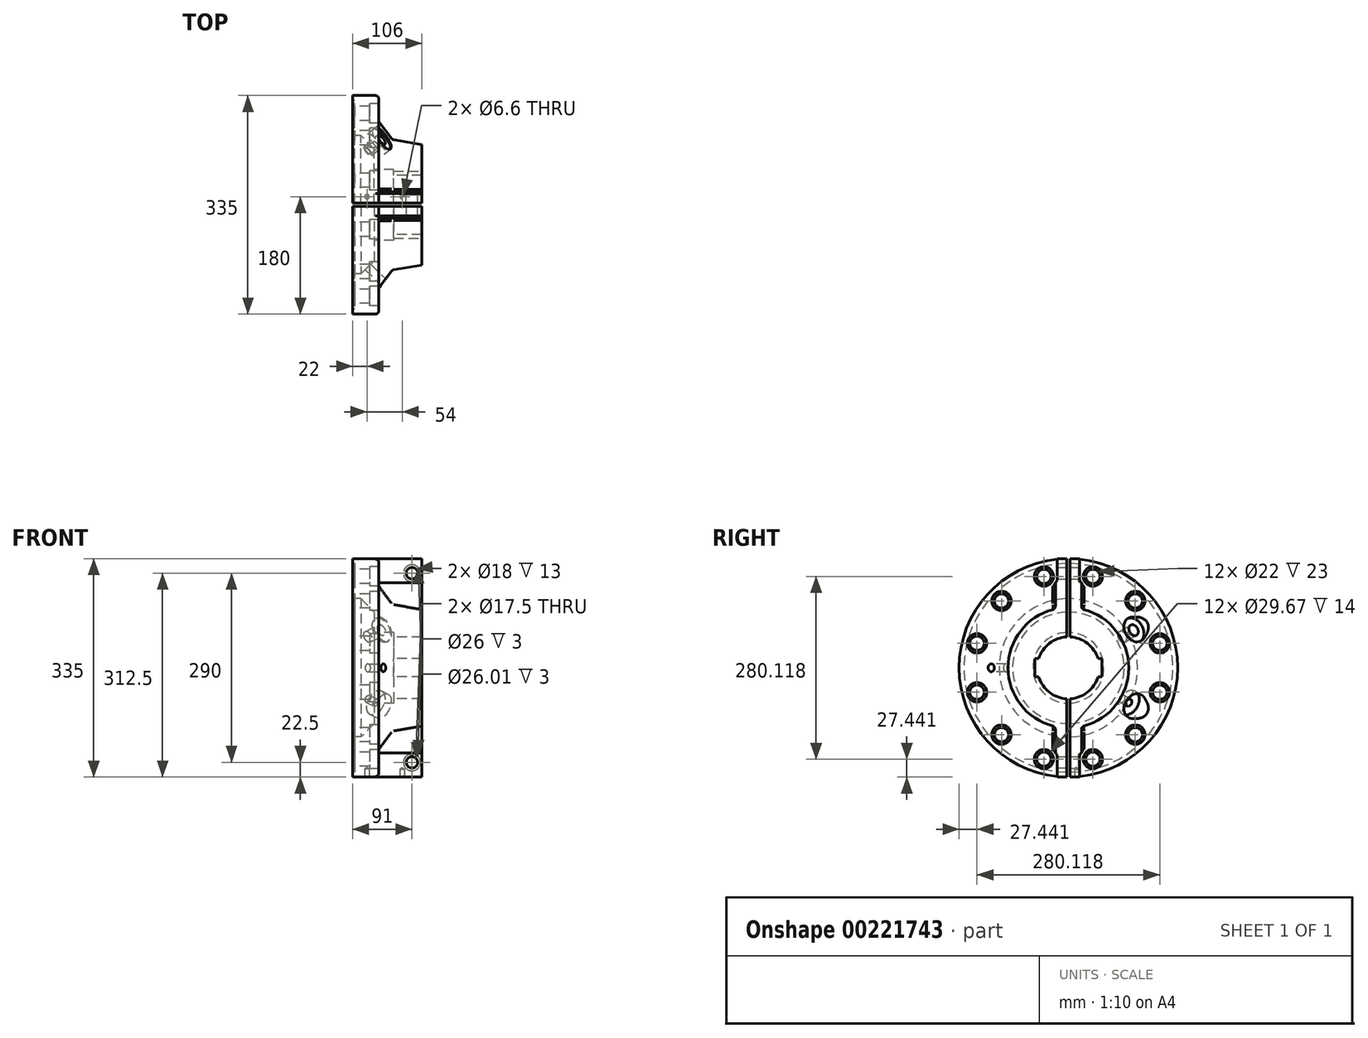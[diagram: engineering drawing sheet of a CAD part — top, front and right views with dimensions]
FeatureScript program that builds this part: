
annotation { "Feature Type Name" : "Feature", "Feature Type Description" : "" }
export const myFeature = defineFeature(function(context is Context, id is Id, definition is map)
    precondition{}
    {
        {
            var Q0;
            Q0=qCreatedBy(makeId("Front.planeOp"),FACE);
            var sketch = newSketch(context, id + "F0", { "sketchPlane" : qUnion([Q0])});
            skLineSegment(sketch, "E0", {"start": v(0, 0) * mm, "end": v(0, 167.5) * mm});
            skLineSegment(sketch, "E1", {"start": v(0, 167.5) * mm, "end": v(40, 167.5) * mm});
            skLineSegment(sketch, "E2", {"start": v(40, 167.5) * mm, "end": v(40, 127.5) * mm});
            skLineSegment(sketch, "E3", {"start": v(40, 127.5) * mm, "end": v(61, 100) * mm});
            skLineSegment(sketch, "E4", {"start": v(61, 100) * mm, "end": v(106, 92.5) * mm});
            skLineSegment(sketch, "E5", {"start": v(106, 92.5) * mm, "end": v(106, 0) * mm});
            skLineSegment(sketch, "E6", {"start": v(0, 0) * mm, "end": v(106, 0) * mm});
            skSolve(sketch);
        }
        {
            var Q0;
            Q0 = qSketchRegion(id + "F0", true);
            var Q1;
            Q1=sQuery(id+"F0.wireOp",EDGE,"E6");
            revolve(context, id + "F1", {"entities" : qUnion([Q0]), "axis" : qUnion([Q1]), "revolveType" : RevolveType.ONE_DIRECTION, "angle" : 180 * degree});
        }
        {
            var Q0;
            Q0=qCreatedBy(makeId("Front.planeOp"),FACE);
            var sketch = newSketch(context, id + "F2", { "sketchPlane" : qUnion([Q0])});
            skLineSegment(sketch, "E7.0", {"start": v(106, -167.5) * mm, "end": v(106, 167.97) * mm});
            skLineSegment(sketch, "E8.0", {"start": v(40, -167.5) * mm, "end": v(106, -167.5) * mm});
            skPoint(sketch, "E9.orphan", {"position": v(40, -167.5) * mm});
            skPoint(sketch, "E10.orphan", {"position": v(106, -92.5) * mm});
            skPoint(sketch, "E11.orphan", {"position": v(106, 92.5) * mm});
            skLineSegment(sketch, "E12.0", {"start": v(40, 167.5) * mm, "end": v(106, 167.5) * mm});
            skPoint(sketch, "E13.orphan", {"position": v(40, 167.5) * mm});
            skLineSegment(sketch, "E14.0", {"start": v(40, -167.5) * mm, "end": v(40, 167.5) * mm});
            skPoint(sketch, "E15.orphan", {"position": v(0, -167.5) * mm});
            skPoint(sketch, "E16.orphan", {"position": v(0, 167.5) * mm});
            skSolve(sketch);
        }
        {
            var Q0;
            Q0 = qSketchRegion(id + "F2", true);
            extrude(context, id + "F3", {"entities" : qUnion([Q0]), "operationType" : NewBodyOperationType.ADD, "depth" : 20 * mm});
        }
        {
            var Q0;
            Q0=makeQuery(id+"F3.boolean.opBoolean","MERGE",FACE,{"derivedFrom":[makeQuery(id+"F1.opRevolve","SWEPT_FACE",FACE,{"disambiguationData":[OSD([sQuery(id+"F0.wireOp",EDGE,"E5")])]}),makeQuery(id+"F3.opExtrude","SWEPT_FACE",FACE,{"disambiguationData":[OSD([sQuery(id+"F2.wireOp",EDGE,"E7.0")])]})]});
            var sketch = newSketch(context, id + "F4", { "sketchPlane" : qUnion([Q0])});
            skLineSegment(sketch, "E17.bottom", {"start": v(-20, -167.5) * mm, "end": v(-17, -167.5) * mm});
            skLineSegment(sketch, "E17.left", {"start": v(-20, -167.5) * mm, "end": v(-20, -130.36) * mm});
            skLineSegment(sketch, "E17.right", {"start": v(-17, -167.5) * mm, "end": v(-17, -137.5) * mm});
            skPoint(sketch, "E18.visualSharp", {"position": v(-17, -121.57) * mm});
            skArc(sketch, "E18.filletArc", {"start": v(-17, -137.5) * mm, "mid": v(-17.78, -133.63) * mm, "end": v(-20, -130.36) * mm});
            skLineSegment(sketch, "E19", {"start": v(0, 0) * mm, "end": v(-51.58, 0) * mm, "construction": true});
            skLineSegment(sketch, "E20.MirrorCS", {"start": v(-17, 167.5) * mm, "end": v(-17, 137.5) * mm});
            skLineSegment(sketch, "E21.MirrorCS", {"start": v(-20, 167.5) * mm, "end": v(-17, 167.5) * mm});
            skLineSegment(sketch, "E22.MirrorCS", {"start": v(-20, 167.5) * mm, "end": v(-20, 130.36) * mm});
            skArc(sketch, "E23.MirrorCS", {"start": v(-17, 137.5) * mm, "mid": v(-17.78, 133.63) * mm, "end": v(-20, 130.36) * mm});
            skSolve(sketch);
        }
        {
            var Q0;
            Q0 = qSketchRegion(id + "F4", true);
            extrude(context, id + "F5", {"entities" : qUnion([Q0]), "operationType" : NewBodyOperationType.REMOVE, "oppositeDirection" : true, "depth" : 66 * mm});
        }
        {
            var Q0;
            Q0=makeQuery(id+"F1.opRevolve","SWEPT_BODY",BODY,{"disambiguationData":[OSD([sQuery(id+"F0.wireOp",EDGE,"E0"),sQuery(id+"F0.wireOp",EDGE,"E1"),sQuery(id+"F0.wireOp",EDGE,"E2"),sQuery(id+"F0.wireOp",EDGE,"E3"),sQuery(id+"F0.wireOp",EDGE,"E4"),sQuery(id+"F0.wireOp",EDGE,"E5"),sQuery(id+"F0.wireOp",EDGE,"E6")])]});
            var Q1;
            Q1=qCreatedBy(makeId("Front.planeOp"),FACE);
            mirror(context, id + "F6", {"entities" : qUnion([Q0]), "mirrorPlane" : qUnion([Q1])});
        }
        {
            var Q0;
            Q0=makeQuery(id+"F6.opPattern","COPY",FACE,{"derivedFrom":makeQuery(id+"F1.opRevolve","SWEPT_FACE",FACE,{"disambiguationData":[OSD([sQuery(id+"F0.wireOp",EDGE,"E0")])]}),"instanceName":"1"});
            var sketch = newSketch(context, id + "F7", { "sketchPlane" : qUnion([Q0])});
            skLineSegment(sketch, "E24.bottom", {"start": v(-2.5, 185) * mm, "end": v(2.5, 185) * mm});
            skLineSegment(sketch, "E24.top", {"start": v(-2.5, -185) * mm, "end": v(2.5, -185) * mm});
            skLineSegment(sketch, "E24.left", {"start": v(-2.5, 185) * mm, "end": v(-2.5, -185) * mm});
            skLineSegment(sketch, "E24.right", {"start": v(2.5, 185) * mm, "end": v(2.5, -185) * mm});
            skPoint(sketch, "E24.middle", {"position": v(0, 0) * mm});
            skSolve(sketch);
        }
        {
            var Q0;
            Q0 = qSketchRegion(id + "F7", true);
            extrude(context, id + "F8", {"entities" : qUnion([Q0]), "operationType" : NewBodyOperationType.REMOVE, "endBound" : BoundingType.THROUGH_ALL, "oppositeDirection" : true, "depth" : 25 * mm});
        }
        {
            var Q0;
            Q0=qCreatedBy(makeId("Top.planeOp"),FACE);
            var sketch = newSketch(context, id + "F9", { "sketchPlane" : qUnion([Q0])});
            skLineSegment(sketch, "E25", {"start": v(0, 0) * mm, "end": v(0, 160) * mm});
            skLineSegment(sketch, "E26", {"start": v(0, 160) * mm, "end": v(3, 160) * mm});
            skLineSegment(sketch, "E27", {"start": v(3, 160) * mm, "end": v(3, 106) * mm});
            skLineSegment(sketch, "E28", {"start": v(3, 106) * mm, "end": v(13, 106) * mm});
            skLineSegment(sketch, "E29", {"start": v(13, 106) * mm, "end": v(33, 85.5) * mm});
            skLineSegment(sketch, "E30", {"start": v(33, 85.5) * mm, "end": v(33, 54.2) * mm});
            skLineSegment(sketch, "E31", {"start": v(33, 54.2) * mm, "end": v(63, 54.2) * mm});
            skLineSegment(sketch, "E32", {"start": v(63, 54.2) * mm, "end": v(63, 47.5) * mm});
            skLineSegment(sketch, "E33", {"start": v(63, 47.5) * mm, "end": v(106, 47.5) * mm});
            skLineSegment(sketch, "E34", {"start": v(106, 47.5) * mm, "end": v(106, 0) * mm});
            skLineSegment(sketch, "E35", {"start": v(106, 0) * mm, "end": v(0, 0) * mm});
            skSolve(sketch);
        }
        {
            var Q0;
            Q0 = qSketchRegion(id + "F9", true);
            var Q1;
            Q1=sQuery(id+"F9.wireOp",EDGE,"E35");
            revolve(context, id + "F10", {"operationType" : NewBodyOperationType.REMOVE, "entities" : qUnion([Q0]), "axis" : qUnion([Q1]), "revolveType" : RevolveType.FULL, "oppositeDirection" : true});
        }
        {
            var Q0;
            Q0=makeQuery(id+"F10.boolean.opBoolean","COPY",FACE,{"disambiguationData":[TD([makeQuery(id+"F8.boolean.opBoolean","COPY",FACE,{"derivedFrom":makeQuery(id+"F8.opExtrude","SWEPT_FACE",FACE,{"disambiguationData":[OSD([sQuery(id+"F7.wireOp",EDGE,"E24.right")])]})})])],"derivedFrom":makeQuery(id+"F10.opRevolve","SWEPT_FACE",FACE,{"disambiguationData":[OSD([sQuery(id+"F9.wireOp",EDGE,"E27")])]})});
            var sketch = newSketch(context, id + "F11", { "sketchPlane" : qUnion([Q0])});
            skCircle(sketch, "E36", {"center": v(37.53, 140.06) * mm, "radius": 11 * mm});
            skLineSegment(sketch, "E37", {"start": v(0, 0) * mm, "end": v(37.53, 140.06) * mm, "construction": true});
            skLineSegment(sketch, "E38", {"start": v(0, 0) * mm, "end": v(0, 41.16) * mm, "construction": true});
            skCircle(sketch, "E39.1.0", {"center": v(-37.53, 140.06) * mm, "radius": 11 * mm});
            skCircle(sketch, "E39.2.0", {"center": v(-102.53, 102.53) * mm, "radius": 11 * mm});
            skCircle(sketch, "E39.3.0", {"center": v(-140.06, 37.53) * mm, "radius": 11 * mm});
            skCircle(sketch, "E39.4.0", {"center": v(-140.06, -37.53) * mm, "radius": 11 * mm});
            skCircle(sketch, "E39.5.0", {"center": v(-102.53, -102.53) * mm, "radius": 11 * mm});
            skCircle(sketch, "E39.6.0", {"center": v(-37.53, -140.06) * mm, "radius": 11 * mm});
            skCircle(sketch, "E39.7.0", {"center": v(37.53, -140.06) * mm, "radius": 11 * mm});
            skCircle(sketch, "E39.8.0", {"center": v(102.53, -102.53) * mm, "radius": 11 * mm});
            skCircle(sketch, "E39.9.0", {"center": v(140.06, -37.53) * mm, "radius": 11 * mm});
            skCircle(sketch, "E39.10.0", {"center": v(140.06, 37.53) * mm, "radius": 11 * mm});
            skCircle(sketch, "E39.11.0", {"center": v(102.53, 102.53) * mm, "radius": 11 * mm});
            skPoint(sketch, "E39.center", {"position": v(0, 0) * mm});
            skCircle(sketch, "E40", {"center": v(37.53, 140.06) * mm, "radius": 14.84 * mm});
            skCircle(sketch, "E41", {"center": v(102.53, 102.53) * mm, "radius": 14.84 * mm});
            skCircle(sketch, "E42", {"center": v(140.06, 37.53) * mm, "radius": 14.84 * mm});
            skCircle(sketch, "E43", {"center": v(140.06, -37.53) * mm, "radius": 14.84 * mm});
            skCircle(sketch, "E44", {"center": v(102.53, -102.53) * mm, "radius": 14.84 * mm});
            skCircle(sketch, "E45", {"center": v(37.53, -140.06) * mm, "radius": 14.84 * mm});
            skCircle(sketch, "E46", {"center": v(-37.53, -140.06) * mm, "radius": 14.84 * mm});
            skCircle(sketch, "E47", {"center": v(-102.53, -102.53) * mm, "radius": 14.84 * mm});
            skCircle(sketch, "E48", {"center": v(-140.06, -37.53) * mm, "radius": 14.84 * mm});
            skCircle(sketch, "E49", {"center": v(-140.06, 37.53) * mm, "radius": 14.84 * mm});
            skCircle(sketch, "E50", {"center": v(-102.53, 102.53) * mm, "radius": 14.84 * mm});
            skCircle(sketch, "E51", {"center": v(-37.53, 140.06) * mm, "radius": 14.84 * mm});
            skSolve(sketch);
        }
        {
            var Q0;
            Q0=makeQuery(id+"F11.imprint","IMPRINT",FACE,{"disambiguationData":[TD([[makeQuery(id+"F11.imprint","IMPRINT",EDGE,{"derivedFrom":sQuery(id+"F11.wireOp",EDGE,"E39.1.0")}),1.0]])]});
            var Q1;
            Q1=makeQuery(id+"F11.imprint","IMPRINT",FACE,{"disambiguationData":[TD([[makeQuery(id+"F11.imprint","IMPRINT",EDGE,{"derivedFrom":sQuery(id+"F11.wireOp",EDGE,"E36")}),1.0]])]});
            var Q2;
            Q2=makeQuery(id+"F11.imprint","IMPRINT",FACE,{"disambiguationData":[TD([[makeQuery(id+"F11.imprint","IMPRINT",EDGE,{"derivedFrom":sQuery(id+"F11.wireOp",EDGE,"E39.11.0")}),1.0]])]});
            var Q3;
            Q3=makeQuery(id+"F11.imprint","IMPRINT",FACE,{"disambiguationData":[TD([[makeQuery(id+"F11.imprint","IMPRINT",EDGE,{"derivedFrom":sQuery(id+"F11.wireOp",EDGE,"E39.10.0")}),1.0]])]});
            var Q4;
            Q4=makeQuery(id+"F11.imprint","IMPRINT",FACE,{"disambiguationData":[TD([[makeQuery(id+"F11.imprint","IMPRINT",EDGE,{"derivedFrom":sQuery(id+"F11.wireOp",EDGE,"E39.8.0")}),1.0]])]});
            var Q5;
            Q5=makeQuery(id+"F11.imprint","IMPRINT",FACE,{"disambiguationData":[TD([[makeQuery(id+"F11.imprint","IMPRINT",EDGE,{"derivedFrom":sQuery(id+"F11.wireOp",EDGE,"E39.7.0")}),1.0]])]});
            var Q6;
            Q6=makeQuery(id+"F11.imprint","IMPRINT",FACE,{"disambiguationData":[TD([[makeQuery(id+"F11.imprint","IMPRINT",EDGE,{"derivedFrom":sQuery(id+"F11.wireOp",EDGE,"E39.6.0")}),1.0]])]});
            var Q7;
            Q7=makeQuery(id+"F11.imprint","IMPRINT",FACE,{"disambiguationData":[TD([[makeQuery(id+"F11.imprint","IMPRINT",EDGE,{"derivedFrom":sQuery(id+"F11.wireOp",EDGE,"E39.5.0")}),1.0]])]});
            var Q8;
            Q8=makeQuery(id+"F6.opPattern","COPY",FACE,{"derivedFrom":makeQuery(id+"F5.boolean.opBoolean","MERGE",FACE,{"derivedFrom":[makeQuery(id+"F1.opRevolve","SWEPT_FACE",FACE,{"disambiguationData":[OSD([sQuery(id+"F0.wireOp",EDGE,"E2")])]}),makeQuery(id+"F5.opExtrude","CAP_FACE",FACE,{"disambiguationData":[OSD([sQuery(id+"F4.wireOp",EDGE,"E17.bottom"),sQuery(id+"F4.wireOp",EDGE,"E17.left"),sQuery(id+"F4.wireOp",EDGE,"E17.right"),sQuery(id+"F4.wireOp",EDGE,"E18.filletArc")])],"isStart":false}),makeQuery(id+"F5.opExtrude","CAP_FACE",FACE,{"disambiguationData":[OSD([sQuery(id+"F4.wireOp",EDGE,"E20.MirrorCS"),sQuery(id+"F4.wireOp",EDGE,"E21.MirrorCS"),sQuery(id+"F4.wireOp",EDGE,"E22.MirrorCS"),sQuery(id+"F4.wireOp",EDGE,"E23.MirrorCS")])],"isStart":false})]}),"instanceName":"1"});
            var Q9;
            Q9=makeQuery(id+"F11.imprint","IMPRINT",FACE,{"disambiguationData":[TD([[makeQuery(id+"F11.imprint","IMPRINT",EDGE,{"derivedFrom":sQuery(id+"F11.wireOp",EDGE,"E39.4.0")}),1.0]])]});
            var Q10;
            Q10=makeQuery(id+"F11.imprint","IMPRINT",FACE,{"disambiguationData":[TD([[makeQuery(id+"F11.imprint","IMPRINT",EDGE,{"derivedFrom":sQuery(id+"F11.wireOp",EDGE,"E39.2.0")}),1.0]])]});
            var Q11;
            Q11=makeQuery(id+"F11.imprint","IMPRINT",FACE,{"disambiguationData":[TD([[makeQuery(id+"F11.imprint","IMPRINT",EDGE,{"derivedFrom":sQuery(id+"F11.wireOp",EDGE,"E39.3.0")}),1.0]])]});
            var Q12;
            Q12=makeQuery(id+"F11.imprint","IMPRINT",FACE,{"disambiguationData":[TD([[makeQuery(id+"F11.imprint","IMPRINT",EDGE,{"derivedFrom":sQuery(id+"F11.wireOp",EDGE,"E39.9.0")}),1.0]])]});
            extrude(context, id + "F12", {"entities" : qUnion([Q0, Q1, Q2, Q3, Q4, Q5, Q6, Q7, Q8, Q9, Q10, Q11, Q12]), "operationType" : NewBodyOperationType.REMOVE, "endBound" : BoundingType.THROUGH_ALL, "oppositeDirection" : true, "depth" : 25 * mm});
        }
        {
            var Q0;
            Q0=qCreatedBy(makeId("Front.planeOp"),FACE);
            var sketch = newSketch(context, id + "F13", { "sketchPlane" : qUnion([Q0])});
            skCircle(sketch, "E52", {"center": v(91, 145) * mm, "radius": 7 * mm});
            skLineSegment(sketch, "E53", {"start": v(2.74, 0) * mm, "end": v(116.17, 0) * mm, "construction": true});
            skCircle(sketch, "E54.MirrorC", {"center": v(91, -145) * mm, "radius": 7 * mm});
            skSolve(sketch);
        }
        {
            var Q0;
            Q0 = qSketchRegion(id + "F13", true);
            extrude(context, id + "F14", {"entities" : qUnion([Q0]), "operationType" : NewBodyOperationType.REMOVE, "depth" : 17 * mm});
        }
        {
            var Q0;
            Q0=makeQuery(id+"F6.opPattern","COPY",FACE,{"derivedFrom":makeQuery(id+"F5.boolean.opBoolean","COPY",FACE,{"derivedFrom":makeQuery(id+"F5.opExtrude","SWEPT_FACE",FACE,{"disambiguationData":[OSD([sQuery(id+"F4.wireOp",EDGE,"E20.MirrorCS")])]})}),"instanceName":"1"});
            var sketch = newSketch(context, id + "F15", { "sketchPlane" : qUnion([Q0])});
            skCircle(sketch, "E55", {"center": v(-91, -145) * mm, "radius": 9 * mm});
            skCircle(sketch, "E56", {"center": v(-91, 145) * mm, "radius": 9 * mm});
            skCircle(sketch, "E57", {"center": v(-91, -145) * mm, "radius": 13 * mm});
            skCircle(sketch, "E58", {"center": v(-91, 145) * mm, "radius": 13 * mm});
            skSolve(sketch);
        }
        {
            var Q0;
            {var subQ0=sQuery(id+"F0.wireOp",EDGE,"E1");var subQ1=sQuery(id+"F0.wireOp",EDGE,"E2");Q0=makeQuery(id+"F3.boolean.opBoolean","SPLIT",EDGE,{"disambiguationData":[topologyDisambiguationEdgeConnected([makeQuery(id+"F1.opRevolve","SWEPT_FACE",FACE,{"disambiguationData":[OSD([subQ0])]}),makeQuery(id+"F1.opRevolve","SWEPT_FACE",FACE,{"disambiguationData":[OSD([subQ1])]})])],"derivedFrom":makeQuery(id+"F1.opRevolve","SWEPT_EDGE",EDGE,{"disambiguationData":[OSD([subQ0,subQ1])]})});}
            var Q1;
            Q1=makeQuery(id+"F1.opRevolve","SWEPT_EDGE",EDGE,{"disambiguationData":[OSD([sQuery(id+"F0.wireOp",EDGE,"E2"),sQuery(id+"F0.wireOp",EDGE,"E3")])]});
            var Q2;
            Q2=makeQuery(id+"F1.opRevolve","SWEPT_EDGE",EDGE,{"disambiguationData":[OSD([sQuery(id+"F0.wireOp",EDGE,"E3"),sQuery(id+"F0.wireOp",EDGE,"E4")])]});
            var Q3;
            Q3=makeQuery(id+"F3.boolean.opBoolean","INTERSECT",EDGE,{"disambiguationData":[OD(0.0)],"derivedFrom":[makeQuery(id+"F1.opRevolve","SWEPT_FACE",FACE,{"disambiguationData":[OSD([sQuery(id+"F0.wireOp",EDGE,"E4")])]}),makeQuery(id+"F3.opExtrude","CAP_FACE",FACE,{"disambiguationData":[OSD([sQuery(id+"F2.wireOp",EDGE,"E7.0"),sQuery(id+"F2.wireOp",EDGE,"E8.0"),sQuery(id+"F2.wireOp",EDGE,"E12.0"),sQuery(id+"F2.wireOp",EDGE,"E14.0")])],"isStart":false})]});
            var Q4;
            Q4=makeQuery(id+"F3.boolean.opBoolean","INTERSECT",EDGE,{"disambiguationData":[OD(1.0)],"derivedFrom":[makeQuery(id+"F1.opRevolve","SWEPT_FACE",FACE,{"disambiguationData":[OSD([sQuery(id+"F0.wireOp",EDGE,"E4")])]}),makeQuery(id+"F3.opExtrude","CAP_FACE",FACE,{"disambiguationData":[OSD([sQuery(id+"F2.wireOp",EDGE,"E7.0"),sQuery(id+"F2.wireOp",EDGE,"E8.0"),sQuery(id+"F2.wireOp",EDGE,"E12.0"),sQuery(id+"F2.wireOp",EDGE,"E14.0")])],"isStart":false})]});
            var Q5;
            Q5=makeQuery(id+"F3.boolean.opBoolean","INTERSECT",EDGE,{"disambiguationData":[OD(0.0)],"derivedFrom":[makeQuery(id+"F1.opRevolve","SWEPT_FACE",FACE,{"disambiguationData":[OSD([sQuery(id+"F0.wireOp",EDGE,"E3")])]}),makeQuery(id+"F3.opExtrude","CAP_FACE",FACE,{"disambiguationData":[OSD([sQuery(id+"F2.wireOp",EDGE,"E7.0"),sQuery(id+"F2.wireOp",EDGE,"E8.0"),sQuery(id+"F2.wireOp",EDGE,"E12.0"),sQuery(id+"F2.wireOp",EDGE,"E14.0")])],"isStart":false})]});
            var Q6;
            Q6=makeQuery(id+"F3.boolean.opBoolean","INTERSECT",EDGE,{"disambiguationData":[OD(1.0)],"derivedFrom":[makeQuery(id+"F1.opRevolve","SWEPT_FACE",FACE,{"disambiguationData":[OSD([sQuery(id+"F0.wireOp",EDGE,"E3")])]}),makeQuery(id+"F3.opExtrude","CAP_FACE",FACE,{"disambiguationData":[OSD([sQuery(id+"F2.wireOp",EDGE,"E7.0"),sQuery(id+"F2.wireOp",EDGE,"E8.0"),sQuery(id+"F2.wireOp",EDGE,"E12.0"),sQuery(id+"F2.wireOp",EDGE,"E14.0")])],"isStart":false})]});
            var Q7;
            {var subQ0=sQuery(id+"F0.wireOp",EDGE,"E1");var subQ1=makeQuery(id+"F1.opRevolve","SWEPT_FACE",FACE,{"disambiguationData":[OSD([subQ0])]});var subQ2=sQuery(id+"F0.wireOp",EDGE,"E2");var subQ3=makeQuery(id+"F1.opRevolve","SWEPT_FACE",FACE,{"disambiguationData":[OSD([subQ2])]});var subQ4=makeQuery(id+"F1.opRevolve","SWEPT_EDGE",EDGE,{"disambiguationData":[OSD([subQ0,subQ2])]});var subQ5=sQuery(id+"F2.wireOp",EDGE,"E14.0");var subQ6=sQuery(id+"F2.wireOp",EDGE,"E12.0");var subQ7=sQuery(id+"F2.wireOp",EDGE,"E8.0");var subQ12=makeQuery(id+"F3.opExtrude","SWEPT_FACE",FACE,{"disambiguationData":[OSD([subQ5])]});Q7=makeQuery(id+"F6.opPattern","COPY",EDGE,{"derivedFrom":makeQuery(id+"F5.boolean.opBoolean","MERGE",EDGE,{"derivedFrom":[makeQuery(id+"F3.boolean.opBoolean","SPLIT",EDGE,{"disambiguationData":[topologyDisambiguationEdgeConnected([subQ1,subQ12]),TD([makeQuery(id+"F3.opExtrude","SWEPT_FACE",FACE,{"disambiguationData":[OSD([subQ6])]})])],"derivedFrom":subQ4}),makeQuery(id+"F3.boolean.opBoolean","SPLIT",EDGE,{"disambiguationData":[topologyDisambiguationEdgeConnected([subQ1,subQ12]),TD([makeQuery(id+"F3.opExtrude","SWEPT_FACE",FACE,{"disambiguationData":[OSD([subQ7])]})])],"derivedFrom":subQ4}),makeQuery(id+"F3.boolean.opBoolean","SPLIT",EDGE,{"disambiguationData":[topologyDisambiguationEdgeConnected([subQ1,subQ3])],"derivedFrom":subQ4})]}),"instanceName":"1"});}
            var Q8;
            Q8=makeQuery(id+"F6.opPattern","COPY",EDGE,{"derivedFrom":makeQuery(id+"F1.opRevolve","SWEPT_EDGE",EDGE,{"disambiguationData":[OSD([sQuery(id+"F0.wireOp",EDGE,"E2"),sQuery(id+"F0.wireOp",EDGE,"E3")])]}),"instanceName":"1"});
            var Q9;
            Q9=makeQuery(id+"F6.opPattern","COPY",EDGE,{"derivedFrom":makeQuery(id+"F1.opRevolve","SWEPT_EDGE",EDGE,{"disambiguationData":[OSD([sQuery(id+"F0.wireOp",EDGE,"E3"),sQuery(id+"F0.wireOp",EDGE,"E4")])]}),"instanceName":"1"});
            var Q10;
            Q10=makeQuery(id+"F6.opPattern","COPY",EDGE,{"derivedFrom":makeQuery(id+"F3.boolean.opBoolean","INTERSECT",EDGE,{"disambiguationData":[OD(0.0)],"derivedFrom":[makeQuery(id+"F1.opRevolve","SWEPT_FACE",FACE,{"disambiguationData":[OSD([sQuery(id+"F0.wireOp",EDGE,"E4")])]}),makeQuery(id+"F3.opExtrude","CAP_FACE",FACE,{"disambiguationData":[OSD([sQuery(id+"F2.wireOp",EDGE,"E7.0"),sQuery(id+"F2.wireOp",EDGE,"E8.0"),sQuery(id+"F2.wireOp",EDGE,"E12.0"),sQuery(id+"F2.wireOp",EDGE,"E14.0")])],"isStart":false})]}),"instanceName":"1"});
            var Q11;
            Q11=makeQuery(id+"F6.opPattern","COPY",EDGE,{"derivedFrom":makeQuery(id+"F3.boolean.opBoolean","INTERSECT",EDGE,{"disambiguationData":[OD(0.0)],"derivedFrom":[makeQuery(id+"F1.opRevolve","SWEPT_FACE",FACE,{"disambiguationData":[OSD([sQuery(id+"F0.wireOp",EDGE,"E3")])]}),makeQuery(id+"F3.opExtrude","CAP_FACE",FACE,{"disambiguationData":[OSD([sQuery(id+"F2.wireOp",EDGE,"E7.0"),sQuery(id+"F2.wireOp",EDGE,"E8.0"),sQuery(id+"F2.wireOp",EDGE,"E12.0"),sQuery(id+"F2.wireOp",EDGE,"E14.0")])],"isStart":false})]}),"instanceName":"1"});
            var Q12;
            Q12=makeQuery(id+"F6.opPattern","COPY",EDGE,{"derivedFrom":makeQuery(id+"F3.boolean.opBoolean","INTERSECT",EDGE,{"disambiguationData":[OD(1.0)],"derivedFrom":[makeQuery(id+"F1.opRevolve","SWEPT_FACE",FACE,{"disambiguationData":[OSD([sQuery(id+"F0.wireOp",EDGE,"E3")])]}),makeQuery(id+"F3.opExtrude","CAP_FACE",FACE,{"disambiguationData":[OSD([sQuery(id+"F2.wireOp",EDGE,"E7.0"),sQuery(id+"F2.wireOp",EDGE,"E8.0"),sQuery(id+"F2.wireOp",EDGE,"E12.0"),sQuery(id+"F2.wireOp",EDGE,"E14.0")])],"isStart":false})]}),"instanceName":"1"});
            var Q13;
            Q13=makeQuery(id+"F6.opPattern","COPY",EDGE,{"derivedFrom":makeQuery(id+"F3.boolean.opBoolean","INTERSECT",EDGE,{"disambiguationData":[OD(1.0)],"derivedFrom":[makeQuery(id+"F1.opRevolve","SWEPT_FACE",FACE,{"disambiguationData":[OSD([sQuery(id+"F0.wireOp",EDGE,"E4")])]}),makeQuery(id+"F3.opExtrude","CAP_FACE",FACE,{"disambiguationData":[OSD([sQuery(id+"F2.wireOp",EDGE,"E7.0"),sQuery(id+"F2.wireOp",EDGE,"E8.0"),sQuery(id+"F2.wireOp",EDGE,"E12.0"),sQuery(id+"F2.wireOp",EDGE,"E14.0")])],"isStart":false})]}),"instanceName":"1"});
            fillet(context, id + "F16", {"entities" : qUnion([Q0, Q1, Q2, Q3, Q4, Q5, Q6, Q7, Q8, Q9, Q10, Q11, Q12, Q13]), "radius" : 5 * mm, "tangentPropagation" : true, "allowEdgeOverflow" : false});
        }
        {
            var Q0;
            {var subQ0=sQuery(id+"F15.wireOp",EDGE,"E56");var subQ1=makeQuery(id+"F6.opPattern","COPY",EDGE,{"derivedFrom":makeQuery(id+"F5.boolean.opBoolean","COPY",EDGE,{"derivedFrom":makeQuery(id+"F5.opExtrude","SWEPT_EDGE",EDGE,{"disambiguationData":[OSD([sQuery(id+"F4.wireOp",EDGE,"E20.MirrorCS"),sQuery(id+"F4.wireOp",EDGE,"E23.MirrorCS")])]})}),"instanceName":"1"});var subQ2=makeQuery(id+"F15.imprint","INTERSECT",VERTEX,{"disambiguationData":[OD(0.0)],"derivedFrom":[subQ1,subQ0]});Q0=makeQuery(id+"F15.imprint","IMPRINT",FACE,{"disambiguationData":[TD([[makeQuery(id+"F15.imprint","IMPRINT",EDGE,{"disambiguationData":[TD([[subQ2,1.0]])],"derivedFrom":subQ0}),1.0]])]});}
            var Q1;
            Q1=makeQuery(id+"F15.imprint","IMPRINT",FACE,{"disambiguationData":[TD([[makeQuery(id+"F15.imprint","IMPRINT",EDGE,{"derivedFrom":sQuery(id+"F15.wireOp",EDGE,"E55")}),1.0]])]});
            var Q2;
            {var subQ0=sQuery(id+"F15.wireOp",EDGE,"E56");var subQ1=makeQuery(id+"F6.opPattern","COPY",EDGE,{"derivedFrom":makeQuery(id+"F5.boolean.opBoolean","COPY",EDGE,{"derivedFrom":makeQuery(id+"F5.opExtrude","SWEPT_EDGE",EDGE,{"disambiguationData":[OSD([sQuery(id+"F4.wireOp",EDGE,"E20.MirrorCS"),sQuery(id+"F4.wireOp",EDGE,"E23.MirrorCS")])]})}),"instanceName":"1"});var subQ2=makeQuery(id+"F15.imprint","INTERSECT",VERTEX,{"disambiguationData":[OD(0.0)],"derivedFrom":[subQ1,subQ0]});Q2=makeQuery(id+"F15.imprint","IMPRINT",FACE,{"disambiguationData":[TD([[makeQuery(id+"F15.imprint","IMPRINT",EDGE,{"disambiguationData":[TD([[subQ2,-1.0]])],"derivedFrom":subQ0}),1.0]])]});}
            extrude(context, id + "F17", {"entities" : qUnion([Q0, Q1, Q2]), "operationType" : NewBodyOperationType.REMOVE, "oppositeDirection" : true, "depth" : 17 * mm, "hasSecondDirection" : true, "secondDirectionOppositeDirection" : false, "secondDirectionDepth" : 25 * mm});
        }
        {
            var Q0;
            {var subQ0=sQuery(id+"F15.wireOp",EDGE,"E56");var subQ1=makeQuery(id+"F6.opPattern","COPY",EDGE,{"derivedFrom":makeQuery(id+"F5.boolean.opBoolean","COPY",EDGE,{"derivedFrom":makeQuery(id+"F5.opExtrude","SWEPT_EDGE",EDGE,{"disambiguationData":[OSD([sQuery(id+"F4.wireOp",EDGE,"E20.MirrorCS"),sQuery(id+"F4.wireOp",EDGE,"E23.MirrorCS")])]})}),"instanceName":"1"});var subQ2=makeQuery(id+"F15.imprint","INTERSECT",VERTEX,{"disambiguationData":[OD(0.0)],"derivedFrom":[subQ1,subQ0]});Q0=makeQuery(id+"F15.imprint","IMPRINT",FACE,{"disambiguationData":[TD([[makeQuery(id+"F15.imprint","IMPRINT",EDGE,{"disambiguationData":[TD([[subQ2,-1.0]])],"derivedFrom":subQ0}),-1.0]])]});}
            var Q1;
            {var subQ0=sQuery(id+"F15.wireOp",EDGE,"E56");var subQ1=makeQuery(id+"F6.opPattern","COPY",EDGE,{"derivedFrom":makeQuery(id+"F5.boolean.opBoolean","COPY",EDGE,{"derivedFrom":makeQuery(id+"F5.opExtrude","SWEPT_EDGE",EDGE,{"disambiguationData":[OSD([sQuery(id+"F4.wireOp",EDGE,"E20.MirrorCS"),sQuery(id+"F4.wireOp",EDGE,"E23.MirrorCS")])]})}),"instanceName":"1"});var subQ2=makeQuery(id+"F15.imprint","INTERSECT",VERTEX,{"disambiguationData":[OD(0.0)],"derivedFrom":[subQ1,subQ0]});Q1=makeQuery(id+"F15.imprint","IMPRINT",FACE,{"disambiguationData":[TD([[makeQuery(id+"F15.imprint","IMPRINT",EDGE,{"disambiguationData":[TD([[subQ2,1.0]])],"derivedFrom":subQ0}),-1.0]])]});}
            var Q2;
            Q2=makeQuery(id+"F15.imprint","IMPRINT",FACE,{"disambiguationData":[TD([[makeQuery(id+"F15.imprint","IMPRINT",EDGE,{"derivedFrom":sQuery(id+"F15.wireOp",EDGE,"E55")}),-1.0]])]});
            extrude(context, id + "F18", {"entities" : qUnion([Q0, Q1, Q2]), "operationType" : NewBodyOperationType.REMOVE, "endBound" : BoundingType.SYMMETRIC, "oppositeDirection" : true, "depth" : 3 * mm});
        }
        {
            var Q0;
            Q0=makeQuery(id+"F11.imprint","IMPRINT",FACE,{"disambiguationData":[TD([[makeQuery(id+"F11.imprint","IMPRINT",EDGE,{"derivedFrom":sQuery(id+"F11.wireOp",EDGE,"E39.1.0")}),-1.0]])]});
            var Q1;
            Q1=makeQuery(id+"F11.imprint","IMPRINT",FACE,{"disambiguationData":[TD([[makeQuery(id+"F11.imprint","IMPRINT",EDGE,{"derivedFrom":sQuery(id+"F11.wireOp",EDGE,"E39.2.0")}),-1.0]])]});
            var Q2;
            Q2=makeQuery(id+"F11.imprint","IMPRINT",FACE,{"disambiguationData":[TD([[makeQuery(id+"F11.imprint","IMPRINT",EDGE,{"derivedFrom":sQuery(id+"F11.wireOp",EDGE,"E39.3.0")}),-1.0]])]});
            var Q3;
            Q3=makeQuery(id+"F11.imprint","IMPRINT",FACE,{"disambiguationData":[TD([[makeQuery(id+"F11.imprint","IMPRINT",EDGE,{"derivedFrom":sQuery(id+"F11.wireOp",EDGE,"E36")}),-1.0]])]});
            var Q4;
            Q4=makeQuery(id+"F11.imprint","IMPRINT",FACE,{"disambiguationData":[TD([[makeQuery(id+"F11.imprint","IMPRINT",EDGE,{"derivedFrom":sQuery(id+"F11.wireOp",EDGE,"E39.11.0")}),-1.0]])]});
            var Q5;
            Q5=makeQuery(id+"F11.imprint","IMPRINT",FACE,{"disambiguationData":[TD([[makeQuery(id+"F11.imprint","IMPRINT",EDGE,{"derivedFrom":sQuery(id+"F11.wireOp",EDGE,"E39.10.0")}),-1.0]])]});
            var Q6;
            Q6=makeQuery(id+"F11.imprint","IMPRINT",FACE,{"disambiguationData":[TD([[makeQuery(id+"F11.imprint","IMPRINT",EDGE,{"derivedFrom":sQuery(id+"F11.wireOp",EDGE,"E39.4.0")}),-1.0]])]});
            var Q7;
            Q7=makeQuery(id+"F11.imprint","IMPRINT",FACE,{"disambiguationData":[TD([[makeQuery(id+"F11.imprint","IMPRINT",EDGE,{"derivedFrom":sQuery(id+"F11.wireOp",EDGE,"E39.5.0")}),-1.0]])]});
            var Q8;
            Q8=makeQuery(id+"F11.imprint","IMPRINT",FACE,{"disambiguationData":[TD([[makeQuery(id+"F11.imprint","IMPRINT",EDGE,{"derivedFrom":sQuery(id+"F11.wireOp",EDGE,"E39.6.0")}),-1.0]])]});
            var Q9;
            Q9=makeQuery(id+"F11.imprint","IMPRINT",FACE,{"disambiguationData":[TD([[makeQuery(id+"F11.imprint","IMPRINT",EDGE,{"derivedFrom":sQuery(id+"F11.wireOp",EDGE,"E39.8.0")}),-1.0]])]});
            var Q10;
            Q10=makeQuery(id+"F11.imprint","IMPRINT",FACE,{"disambiguationData":[TD([[makeQuery(id+"F11.imprint","IMPRINT",EDGE,{"derivedFrom":sQuery(id+"F11.wireOp",EDGE,"E39.9.0")}),-1.0]])]});
            var Q11;
            Q11=makeQuery(id+"F11.imprint","IMPRINT",FACE,{"disambiguationData":[TD([[makeQuery(id+"F11.imprint","IMPRINT",EDGE,{"derivedFrom":sQuery(id+"F11.wireOp",EDGE,"E39.7.0")}),-1.0]])]});
            var Q12;
            Q12=makeQuery(id+"F6.opPattern","COPY",FACE,{"derivedFrom":makeQuery(id+"F5.boolean.opBoolean","MERGE",FACE,{"derivedFrom":[makeQuery(id+"F1.opRevolve","SWEPT_FACE",FACE,{"disambiguationData":[OSD([sQuery(id+"F0.wireOp",EDGE,"E2")])]}),makeQuery(id+"F5.opExtrude","CAP_FACE",FACE,{"disambiguationData":[OSD([sQuery(id+"F4.wireOp",EDGE,"E17.bottom"),sQuery(id+"F4.wireOp",EDGE,"E17.left"),sQuery(id+"F4.wireOp",EDGE,"E17.right"),sQuery(id+"F4.wireOp",EDGE,"E18.filletArc")])],"isStart":false}),makeQuery(id+"F5.opExtrude","CAP_FACE",FACE,{"disambiguationData":[OSD([sQuery(id+"F4.wireOp",EDGE,"E20.MirrorCS"),sQuery(id+"F4.wireOp",EDGE,"E21.MirrorCS"),sQuery(id+"F4.wireOp",EDGE,"E22.MirrorCS"),sQuery(id+"F4.wireOp",EDGE,"E23.MirrorCS")])],"isStart":false})]}),"instanceName":"1"});
            extrude(context, id + "F19", {"entities" : qUnion([Q0, Q1, Q2, Q3, Q4, Q5, Q6, Q7, Q8, Q9, Q10, Q11]), "operationType" : NewBodyOperationType.REMOVE, "endBound" : BoundingType.THROUGH_ALL, "oppositeDirection" : true, "depth" : 23 * mm, "hasSecondDirection" : true, "secondDirectionOppositeDirection" : true, "secondDirectionBoundEntityFace" : qUnion([Q12]), "secondDirectionDepth" : 23 * mm});
        }
        {
            var Q0;
            Q0=makeQuery(id+"F3.boolean.opBoolean","MERGE",FACE,{"derivedFrom":[makeQuery(id+"F1.opRevolve","SWEPT_FACE",FACE,{"disambiguationData":[OSD([sQuery(id+"F0.wireOp",EDGE,"E5")])]}),makeQuery(id+"F3.opExtrude","SWEPT_FACE",FACE,{"disambiguationData":[OSD([sQuery(id+"F2.wireOp",EDGE,"E7.0")])]})]});
            var sketch = newSketch(context, id + "F20", { "sketchPlane" : qUnion([Q0])});
            skLineSegment(sketch, "E59.bottom", {"start": v(-51.4, -14) * mm, "end": v(51.4, -14) * mm});
            skLineSegment(sketch, "E59.top", {"start": v(-51.4, 14) * mm, "end": v(51.4, 14) * mm});
            skLineSegment(sketch, "E59.left", {"start": v(-51.4, -14) * mm, "end": v(-51.4, 14) * mm});
            skLineSegment(sketch, "E59.right", {"start": v(51.4, -14) * mm, "end": v(51.4, 14) * mm});
            skSolve(sketch);
        }
        {
            var Q0;
            Q0 = qSketchRegion(id + "F20", true);
            extrude(context, id + "F21", {"entities" : qUnion([Q0]), "operationType" : NewBodyOperationType.REMOVE, "endBound" : BoundingType.THROUGH_ALL, "oppositeDirection" : true, "depth" : 25 * mm});
        }
        {
            var Q0;
            Q0=makeQuery(id+"F6.opPattern","COPY",FACE,{"derivedFrom":makeQuery(id+"F3.opExtrude","SWEPT_FACE",FACE,{"disambiguationData":[OSD([sQuery(id+"F2.wireOp",EDGE,"E8.0")])]}),"instanceName":"1"});
            var sketch = newSketch(context, id + "F22", { "sketchPlane" : qUnion([Q0])});
            skCircle(sketch, "E60", {"center": v(76, -12.5) * mm, "radius": 3 * mm});
            skCircle(sketch, "E61", {"center": v(22, -12.5) * mm, "radius": 3 * mm});
            skSolve(sketch);
        }
        {
            var Q0;
            Q0 = qSketchRegion(id + "F22", true);
            extrude(context, id + "F23", {"entities" : qUnion([Q0]), "operationType" : NewBodyOperationType.REMOVE, "oppositeDirection" : true, "depth" : 10 * mm});
        }
        {
            var Q0;
            Q0=qCreatedBy(makeId("Top.planeOp"),FACE);
            var sketch = newSketch(context, id + "F24", { "sketchPlane" : qUnion([Q0])});
            skLineSegment(sketch, "E62.MirrorCS", {"start": v(13.28, -106.06) * mm, "end": v(33.08, -85.77) * mm});
            skLineSegment(sketch, "E63.MirrorCS", {"start": v(23.65, -95.44) * mm, "end": v(67.75, -138.46) * mm, "construction": true});
            skSolve(sketch);
        }
        {
            var Q0;
            Q0=sQuery(id+"F24.wireOp",EDGE,"E63.MirrorCS");
            var Q1;
            Q1=sQuery(id+"F24.wireOp",VERTEX,"E63.MirrorCS.end");
            cPlane(context, id + "F25", {"entities" : qUnion([Q0, Q1]), "cplaneType" : CPlaneType.LINE_POINT, "offset" : 25 * mm, "width" : 150 * mm, "height" : 150 * mm});
        }
        {
            var Q0;
            Q0=qCreatedBy(id+"F25.planeOp",FACE);
            var sketch = newSketch(context, id + "F26", { "sketchPlane" : qUnion([Q0])});
            skCircle(sketch, "E64", {"center": v(-51.8, 0) * mm, "radius": 6 * mm});
            skSolve(sketch);
        }
        {
            var Q0;
            Q0 = qSketchRegion(id + "F26", true);
            extrude(context, id + "F27", {"entities" : qUnion([Q0]), "endBound" : BoundingType.THROUGH_ALL, "oppositeDirection" : true, "depth" : 25 * mm});
        }
        {
            var Q0;
            Q0=makeQuery(id+"F27.opExtrude","SWEPT_BODY",BODY,{"disambiguationData":[OSD([sQuery(id+"F26.wireOp",EDGE,"E64")])]});
            var Q1;
            Q1=sQuery(id+"F9.wireOp",EDGE,"E35");
            transform(context, id + "F28", {"entities" : qUnion([Q0]), "transformType" : TransformType.ROTATION, "transformAxis" : qUnion([Q1]), "angle" : 150 * degree, "makeCopy" : true});
        }
        {
            var Q0;
            Q0=makeQuery(id+"F27.opExtrude","SWEPT_BODY",BODY,{"disambiguationData":[OSD([sQuery(id+"F26.wireOp",EDGE,"E64")])]});
            var Q1;
            Q1=sQuery(id+"F9.wireOp",EDGE,"E35");
            transform(context, id + "F29", {"entities" : qUnion([Q0]), "transformType" : TransformType.ROTATION, "transformAxis" : qUnion([Q1]), "angle" : 210 * degree, "makeCopy" : true});
        }
        {
            var Q0;
            Q0=makeQuery(id+"F27.opExtrude","SWEPT_BODY",BODY,{"disambiguationData":[OSD([sQuery(id+"F26.wireOp",EDGE,"E64")])]});
            var Q1;
            Q1=makeQuery(id+"F1.opRevolve","SWEPT_BODY",BODY,{"disambiguationData":[OSD([sQuery(id+"F0.wireOp",EDGE,"E0"),sQuery(id+"F0.wireOp",EDGE,"E1"),sQuery(id+"F0.wireOp",EDGE,"E2"),sQuery(id+"F0.wireOp",EDGE,"E3"),sQuery(id+"F0.wireOp",EDGE,"E4"),sQuery(id+"F0.wireOp",EDGE,"E5"),sQuery(id+"F0.wireOp",EDGE,"E6")])]});
            booleanBodies(context, id + "F30", {"operationType" : BooleanOperationType.SUBTRACTION, "tools" : qUnion([Q0]), "targets" : qUnion([Q1])});
        }
        {
            var Q0;
            Q0=makeQuery(id+"F29.opPattern","COPY",FACE,{"derivedFrom":makeQuery(id+"F27.opExtrude","CAP_FACE",FACE,{"disambiguationData":[OSD([sQuery(id+"F26.wireOp",EDGE,"E64")])],"isStart":true}),"instanceName":"1"});
            var sketch = newSketch(context, id + "F31", { "sketchPlane" : qUnion([Q0])});
            skCircle(sketch, "E65", {"center": v(40.32, -32.52) * mm, "radius": 6 * mm});
            skCircle(sketch, "E66", {"center": v(40.32, -32.52) * mm, "radius": 20 * mm});
            skSolve(sketch);
        }
        {
            var Q0;
            Q0=makeQuery(id+"F28.opPattern","COPY",FACE,{"derivedFrom":makeQuery(id+"F27.opExtrude","CAP_FACE",FACE,{"disambiguationData":[OSD([sQuery(id+"F26.wireOp",EDGE,"E64")])],"isStart":true}),"instanceName":"1"});
            var sketch = newSketch(context, id + "F32", { "sketchPlane" : qUnion([Q0])});
            skCircle(sketch, "E67", {"center": v(40.32, 32.52) * mm, "radius": 9 * mm});
            skCircle(sketch, "E68", {"center": v(40.32, 32.52) * mm, "radius": 20 * mm});
            skSolve(sketch);
        }
        {
            var Q0;
            Q0=makeQuery(id+"F31.imprint","IMPRINT",FACE,{"disambiguationData":[TD([[makeQuery(id+"F31.imprint","IMPRINT",EDGE,{"derivedFrom":makeQuery(id+"F29.opPattern","COPY",EDGE,{"derivedFrom":makeQuery(id+"F27.opExtrude","CAP_EDGE",EDGE,{"disambiguationData":[OSD([sQuery(id+"F26.wireOp",EDGE,"E64")])],"isStart":true}),"instanceName":"1"})}),1.0]])]});
            var Q1;
            Q1=makeQuery(id+"F31.imprint","IMPRINT",FACE,{"disambiguationData":[TD([[makeQuery(id+"F31.imprint","IMPRINT",EDGE,{"derivedFrom":sQuery(id+"F31.wireOp",EDGE,"E65")}),1.0]])]});
            extrude(context, id + "F33", {"entities" : qUnion([Q0, Q1]), "operationType" : NewBodyOperationType.REMOVE, "endBound" : BoundingType.THROUGH_ALL, "oppositeDirection" : true, "depth" : 25 * mm});
        }
        {
            var Q0;
            Q0=makeQuery(id+"F32.imprint","IMPRINT",FACE,{"disambiguationData":[TD([[makeQuery(id+"F32.imprint","IMPRINT",EDGE,{"derivedFrom":sQuery(id+"F32.wireOp",EDGE,"E67")}),1.0]])]});
            var Q1;
            Q1=makeQuery(id+"F32.imprint","IMPRINT",FACE,{"disambiguationData":[TD([[makeQuery(id+"F32.imprint","IMPRINT",EDGE,{"derivedFrom":makeQuery(id+"F28.opPattern","COPY",EDGE,{"derivedFrom":makeQuery(id+"F27.opExtrude","CAP_EDGE",EDGE,{"disambiguationData":[OSD([sQuery(id+"F26.wireOp",EDGE,"E64")])],"isStart":true}),"instanceName":"1"})}),1.0]])]});
            extrude(context, id + "F34", {"entities" : qUnion([Q0, Q1]), "operationType" : NewBodyOperationType.REMOVE, "endBound" : BoundingType.THROUGH_ALL, "oppositeDirection" : true, "depth" : 25 * mm});
        }
        {
            var Q0;
            Q0 = qSketchRegion(id + "F31", true);
            extrude(context, id + "F35", {"entities" : qUnion([Q0]), "operationType" : NewBodyOperationType.REMOVE, "oppositeDirection" : true, "depth" : 45 * mm});
        }
        {
            var Q0;
            Q0 = qSketchRegion(id + "F32", true);
            extrude(context, id + "F36", {"entities" : qUnion([Q0]), "operationType" : NewBodyOperationType.REMOVE, "oppositeDirection" : true, "depth" : 33 * mm});
        }
        {
            var Q0;
            Q0=sQuery(id+"F15.wireOp",VERTEX,"E55.center");
            var Q1;
            Q1=sQuery(id+"F15.wireOp",VERTEX,"E56.center");
            var Q2;
            Q2=makeQuery(id+"F1.opRevolve","SWEPT_BODY",BODY,{"disambiguationData":[OSD([sQuery(id+"F0.wireOp",EDGE,"E0"),sQuery(id+"F0.wireOp",EDGE,"E1"),sQuery(id+"F0.wireOp",EDGE,"E2"),sQuery(id+"F0.wireOp",EDGE,"E3"),sQuery(id+"F0.wireOp",EDGE,"E4"),sQuery(id+"F0.wireOp",EDGE,"E5"),sQuery(id+"F0.wireOp",EDGE,"E6")])]});
            hole(context, id + "F37", {"style" : HoleStyle.SIMPLE, "endStyle" : HoleEndStyle.THROUGH, "standardTappedOrClearance" : lookupTablePath({ "standard" : "ISO", "fit" : "Normal", "size" : "M16", "type" : "Clearance" }), "standardBlindInLast" : lookupTablePath({ "fit" : "Standard", "standard" : "ISO", "size" : "M16", "type" : "Clearance" }), "holeDiameter" : 17.5 * mm, "isTappedThrough" : true, "tappedDepth" : 12 * mm, "tapClearance" : 3, "locations" : qUnion([Q0, Q1]), "scope" : qUnion([Q2])});
        }
        {
            var Q0;
            Q0=sQuery(id+"F22.wireOp",VERTEX,"E61.center");
            var Q1;
            Q1=sQuery(id+"F22.wireOp",VERTEX,"E60.center");
            var Q2;
            Q2=makeQuery(id+"F6.opPattern","COPY",BODY,{"derivedFrom":makeQuery(id+"F1.opRevolve","SWEPT_BODY",BODY,{"disambiguationData":[OSD([sQuery(id+"F0.wireOp",EDGE,"E0"),sQuery(id+"F0.wireOp",EDGE,"E1"),sQuery(id+"F0.wireOp",EDGE,"E2"),sQuery(id+"F0.wireOp",EDGE,"E3"),sQuery(id+"F0.wireOp",EDGE,"E4"),sQuery(id+"F0.wireOp",EDGE,"E5"),sQuery(id+"F0.wireOp",EDGE,"E6")])]}),"instanceName":"1"});
            hole(context, id + "F38", {"style" : HoleStyle.SIMPLE, "endStyle" : HoleEndStyle.BLIND, "standardTappedOrClearance" : lookupTablePath({ "standard" : "ISO", "fit" : "Normal", "size" : "M6", "type" : "Clearance" }), "standardBlindInLast" : lookupTablePath({ "fit" : "Standard", "standard" : "ISO", "size" : "M6", "type" : "Clearance" }), "holeDiameter" : 6.6 * mm, "holeDepth" : 12 * mm, "isTappedThrough" : true, "tappedDepth" : 12 * mm, "tapClearance" : 3, "locations" : qUnion([Q0, Q1]), "scope" : qUnion([Q2])});
        }
    });
